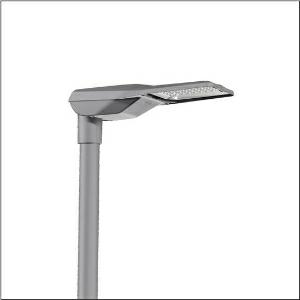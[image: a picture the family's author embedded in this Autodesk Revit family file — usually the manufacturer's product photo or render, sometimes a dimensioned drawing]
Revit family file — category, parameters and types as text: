
# Revit family: streetlight_sl_21_iq_mini___stw1_0a_5xe2e61g08hb_1142
name_source: partatom
category: Lighting Fixtures
units: mm (PartAtom-declared; Revit-internal decimal feet)

## family parameters
Cut with Voids When Loaded = No
Host = Face
Light Source = No
Part Type = Normal
Room Calculation Point = No
Round Connector Dimension = Use Diameter
Shared = No

## types (1)
- --- (1 x LED, 8480 lm, 70.9 W, 2700K)
    Apparent Load = 71 VA
    CIE Flux Codes = 38 75 98 100 100
    Color Rendering = 70
    Color Temperature = 2700K
    Default Elevation = 1800 mm
    Description = Streetlight SL 21 mini, mast luminaire, primary light control with lens, of PMMA, primary optical cover: cover, of toughened safety glass, transparent, light distribution: STW1.0a, light emission: direct distribution, primary light characteristic: asymmetric, installation type: post-top, side-entry, LED, High Power LED, rated luminous flux: 8.480lm, luminous efficacy: 120lm/W, light colour: 727, colour temperature: 2700K, control gear: ECG iQ, control: Street-Remote, Auto-Match, Temp-Guard, Lumen-Switch, Night-Set, Smart-Wire, Light-Fading, Desk-Remote (wireless, voltage-free reading and setting of iQ features in the workshop via application-optimized NFC function/RFID function), optimised constant luminous flux control (CLO 2.0), mains connection: 220..240V, AC, 50/60Hz, start of lifetime: 71W, end of lifetime: 75W, reduction: 31W, luminaire housing, of diecast aluminium, powder-coated, Siteco® metallic grey (DB 702S), corrosivity category C5 according to DIN EN ISO 12944, length: 628mm, width: 235mm, height: 110mm, spigot size: 60/76mm (post-top) and 42/60/76mm (side-entry), mast flange for spigot size: 42mm: 5XC10008XM4, 60mm: 5XC10008XM2, 76/60mm: 5XC10108XM1, protection rating (complete): IP66, insulation class (complete): insulation class II (safety insulation), certification: CE, ENEC, VDE, impact resistance: IK09, permissible operating ambient temperature for outdoor applications: -40..+50°C, standard-compliant lighting for roads and squares, packaging unit: 1 piece

Light Distribution: STW1.0a
    Height = 110 mm
    Lamp = 1 x LED
    Lamp Light Flux = 8480 lm
    Lamp Power = 70.9 W
    Lamp count = 1
    Length = 625 mm
    Luminous efficacy = 120 lm/W
    Manufacturer = Siteco
    ModVariant = No
    Model = 5XE2E61G08HB
    Number of Poles = 1
    OnlyDefault = Yes
    Power Factor = 1
    Product Name = Streetlight SL 21 iQ mini | STW1.0a
    Product group = mast luminaire | pylon top
    ProductGroupID = 6100
    Protection Class = Protection class II
    Protection Degree = IP 66
    RLX_Detail_Level = 1
    RlxData = <blob elided: 92141 chars, md5=9202413a>
    Socket = socket
    Standby Power = 0 W
    System Light Flux = 8480 lm
    System Power = 71 W
    Type Comments = factory setting: luminous flux: 100 % | dim-lin: 254 | 711 mA
    Type Image = l_1003519.jpg
    URL = http://relux.com
    VarID = @adj_069151
    Voltage = 0 V
    Weight = 0.00 kg
    Width = 234 mm

## geometry (parser evidence)
native form markers: Blend x4, Sweep x9
no freeform markers — native parametric forms only
